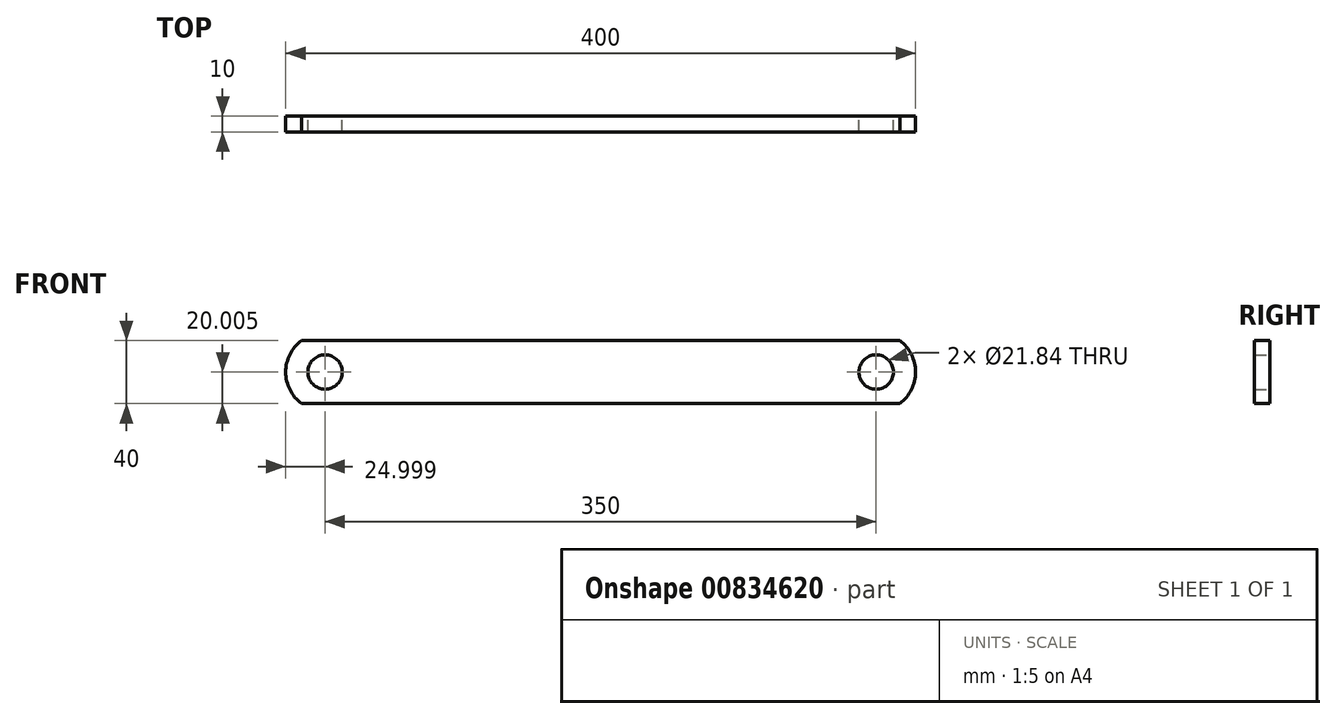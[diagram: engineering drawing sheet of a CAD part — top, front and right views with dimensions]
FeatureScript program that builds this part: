
annotation { "Feature Type Name" : "Feature", "Feature Type Description" : "" }
export const myFeature = defineFeature(function(context is Context, id is Id, definition is map)
    precondition{}
    {
        {
            var Q0;
            Q0=qCreatedBy(makeId("Front.planeOp"),FACE);
            var sketch = newSketch(context, id + "F0", { "sketchPlane" : qUnion([Q0])});
            skLineSegment(sketch, "E0", {"start": v(-184.01, 30.65) * mm, "end": v(195.99, 30.65) * mm});
            skLineSegment(sketch, "E1", {"start": v(195.99, -9.35) * mm, "end": v(-184.01, -9.35) * mm});
            skCircle(sketch, "E2", {"center": v(-169.01, 10.65) * mm, "radius": 10.92 * mm});
            skArc(sketch, "E3", {"start": v(-184.01, 30.65) * mm, "mid": v(-194.01, 10.65) * mm, "end": v(-184.01, -9.35) * mm});
            skLineSegment(sketch, "E4.0", {"start": v(5.99, 30.65) * mm, "end": v(5.99, -9.35) * mm});
            skCircle(sketch, "E5.MirrorC", {"center": v(180.99, 10.65) * mm, "radius": 10.92 * mm});
            skArc(sketch, "E6.MirrorCS", {"start": v(195.99, 30.65) * mm, "mid": v(205.99, 10.65) * mm, "end": v(195.99, -9.35) * mm});
            skPoint(sketch, "E7.orphan", {"position": v(205.99, -9.35) * mm});
            skPoint(sketch, "E8.orphan", {"position": v(205.99, 30.65) * mm});
            skSolve(sketch);
        }
        {
            var Q0;
            Q0 = qSketchRegion(id + "F0", true);
            extrude(context, id + "F1", {"entities" : qUnion([Q0]), "depth" : 10 * mm, "offsetDistance" : 25 * mm});
        }
    });
